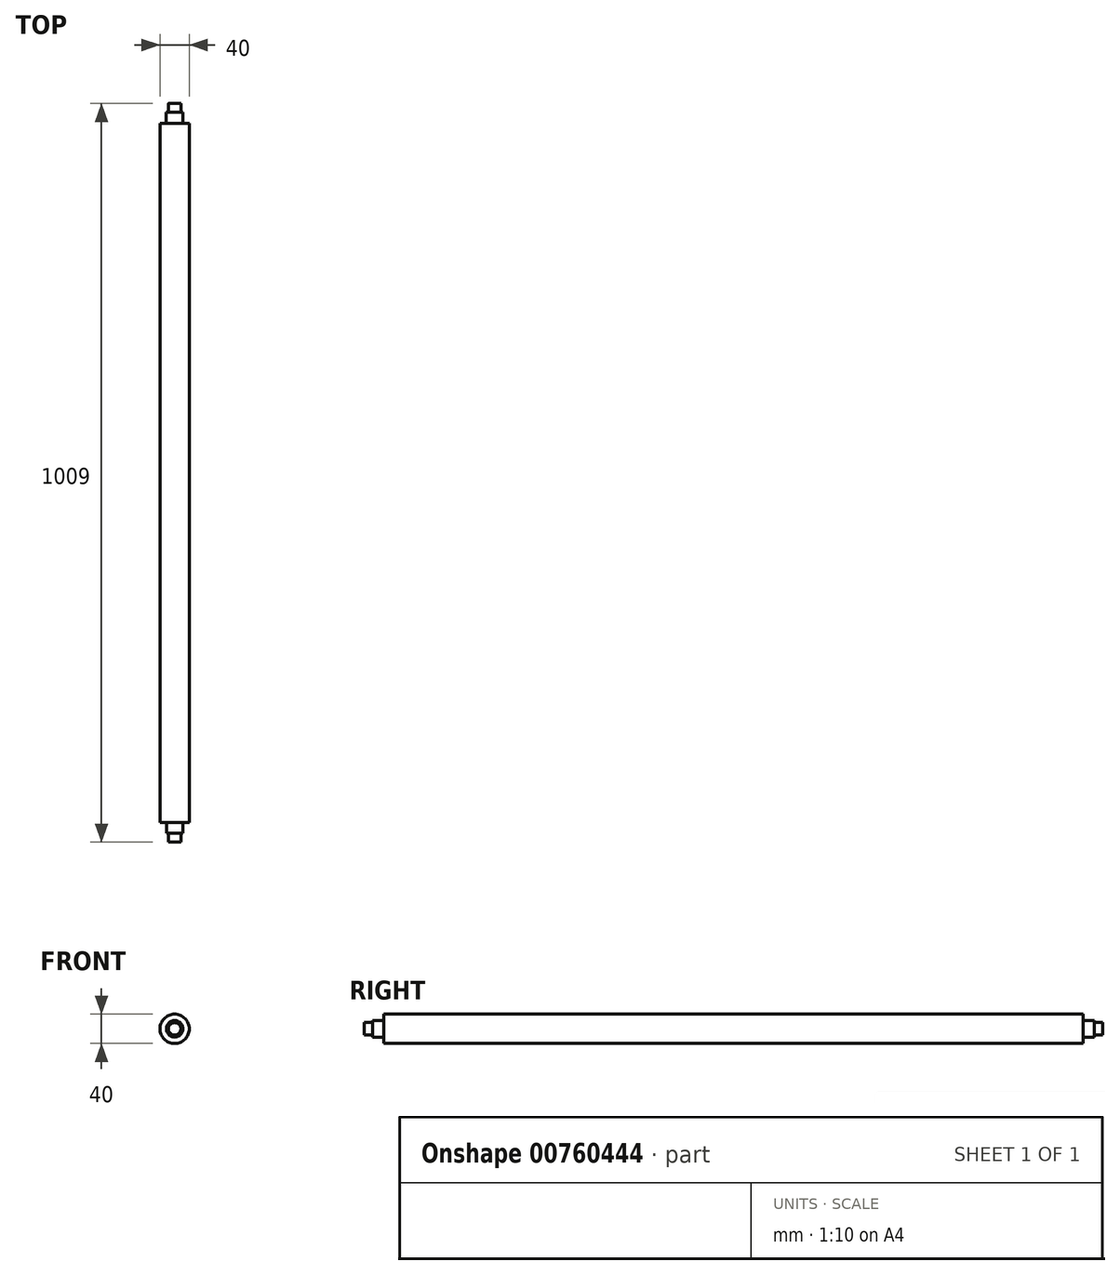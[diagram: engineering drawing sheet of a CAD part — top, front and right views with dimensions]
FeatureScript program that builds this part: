
annotation { "Feature Type Name" : "Feature", "Feature Type Description" : "" }
export const myFeature = defineFeature(function(context is Context, id is Id, definition is map)
    precondition{}
    {
        {
            var Q0;
            Q0=qCreatedBy(makeId("Front.planeOp"),FACE);
            var sketch = newSketch(context, id + "F0", { "sketchPlane" : qUnion([Q0])});
            skCircle(sketch, "E0", {"center": v(0, 0) * mm, "radius": 20 * mm});
            skSolve(sketch);
        }
        {
            var Q0;
            Q0 = qSketchRegion(id + "F0", true);
            extrude(context, id + "F1", {"entities" : qUnion([Q0]), "depth" : 955 * mm, "offsetDistance" : 25 * mm});
        }
        {
            var Q0;
            Q0=makeQuery(id+"F1.opExtrude","CAP_FACE",FACE,{"disambiguationData":[OSD([sQuery(id+"F0.wireOp",EDGE,"E0")])],"isStart":false});
            var sketch = newSketch(context, id + "F2", { "sketchPlane" : qUnion([Q0])});
            skCircle(sketch, "E1", {"center": v(0, 0) * mm, "radius": 11.25 * mm});
            skSolve(sketch);
        }
        {
            var Q0;
            Q0 = qSketchRegion(id + "F2", true);
            extrude(context, id + "F3", {"entities" : qUnion([Q0]), "operationType" : NewBodyOperationType.ADD, "depth" : 15 * mm, "offsetDistance" : 25 * mm});
        }
        {
            var Q0;
            Q0=makeQuery(id+"F1.opExtrude","CAP_FACE",FACE,{"disambiguationData":[OSD([sQuery(id+"F0.wireOp",EDGE,"E0")])],"isStart":true});
            var sketch = newSketch(context, id + "F4", { "sketchPlane" : qUnion([Q0])});
            skCircle(sketch, "E2", {"center": v(0, 0) * mm, "radius": 11.5 * mm});
            skSolve(sketch);
        }
        {
            var Q0;
            Q0 = qSketchRegion(id + "F4", true);
            extrude(context, id + "F5", {"entities" : qUnion([Q0]), "operationType" : NewBodyOperationType.ADD, "depth" : 15 * mm, "offsetDistance" : 25 * mm});
        }
        {
            var Q0;
            Q0=makeQuery(id+"F5.opExtrude","CAP_FACE",FACE,{"disambiguationData":[OSD([sQuery(id+"F4.wireOp",EDGE,"E2")])],"isStart":false});
            var sketch = newSketch(context, id + "F6", { "sketchPlane" : qUnion([Q0])});
            skCircle(sketch, "E3", {"center": v(0, 0) * mm, "radius": 8.5 * mm});
            skSolve(sketch);
        }
        {
            var Q0;
            Q0 = qSketchRegion(id + "F6", true);
            extrude(context, id + "F7", {"entities" : qUnion([Q0]), "operationType" : NewBodyOperationType.ADD, "depth" : 12 * mm, "offsetDistance" : 25 * mm});
        }
        {
            var Q0;
            Q0=makeQuery(id+"F3.opExtrude","CAP_FACE",FACE,{"disambiguationData":[OSD([sQuery(id+"F2.wireOp",EDGE,"E1")])],"isStart":false});
            var sketch = newSketch(context, id + "F8", { "sketchPlane" : qUnion([Q0])});
            skCircle(sketch, "E4", {"center": v(0, 0) * mm, "radius": 8.5 * mm});
            skSolve(sketch);
        }
        {
            var Q0;
            Q0 = qSketchRegion(id + "F8", true);
            extrude(context, id + "F9", {"entities" : qUnion([Q0]), "operationType" : NewBodyOperationType.ADD, "depth" : 12 * mm, "offsetDistance" : 25 * mm});
        }
    });
